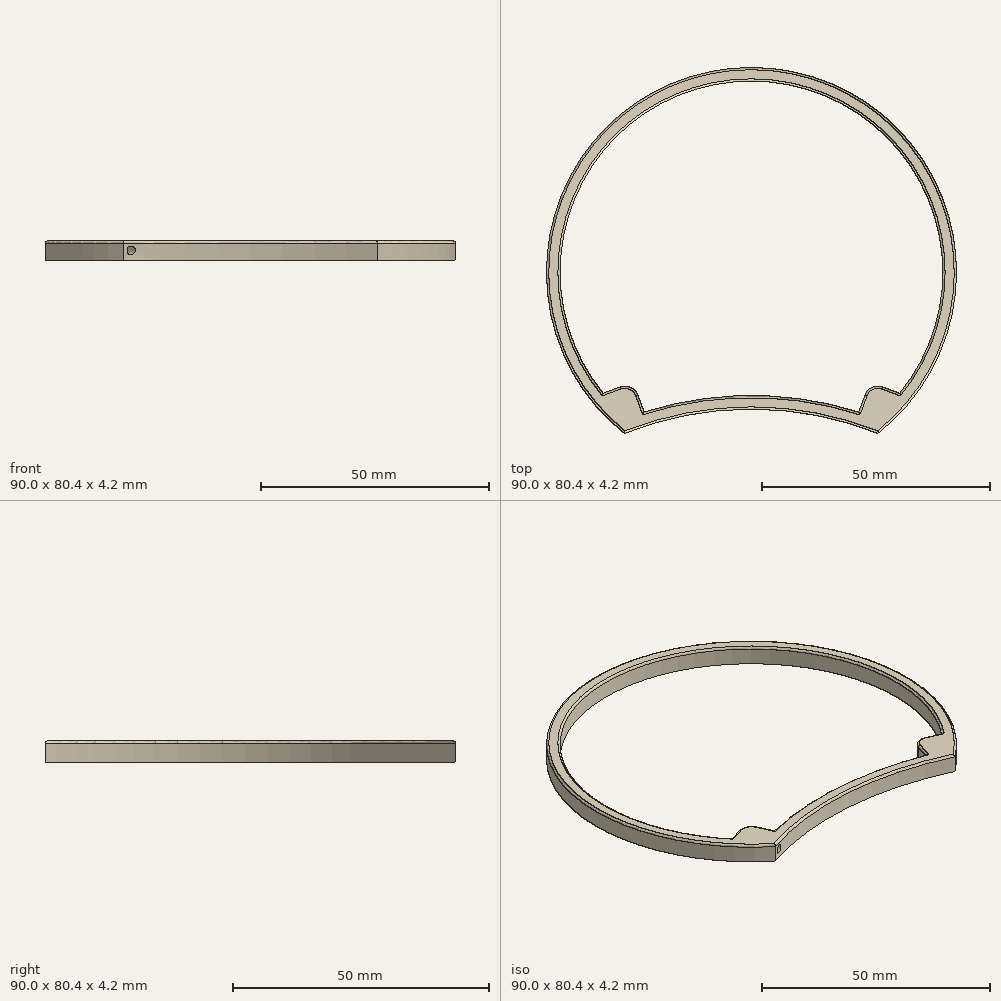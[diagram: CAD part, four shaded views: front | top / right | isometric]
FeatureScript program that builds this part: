
annotation { "Feature Type Name" : "Feature", "Feature Type Description" : "" }
export const myFeature = defineFeature(function(context is Context, id is Id, definition is map)
    precondition{}
    {
        {
            var Q0;
            Q0=qCreatedBy(makeId("Front.planeOp"),FACE);
            var sketch = newSketch(context, id + "F0", { "sketchPlane" : qUnion([Q0])});
            skLineSegment(sketch, "E0.bottom", {"start": v(42, 4.2) * mm, "end": v(45, 4.2) * mm});
            skLineSegment(sketch, "E0.top", {"start": v(42, 0) * mm, "end": v(45, 0) * mm});
            skLineSegment(sketch, "E0.left", {"start": v(42, 4.2) * mm, "end": v(42, 0) * mm});
            skLineSegment(sketch, "E0.right", {"start": v(45, 4.2) * mm, "end": v(45, 0) * mm});
            skLineSegment(sketch, "E1", {"start": v(0, 23.86) * mm, "end": v(0, -32.38) * mm, "construction": true});
            skSolve(sketch);
        }
        {
            var Q0;
            Q0=makeQuery(id+"F0.imprint","IMPRINT",FACE,{"disambiguationData":[TD([[makeQuery(id+"F0.imprint","IMPRINT",EDGE,{"derivedFrom":sQuery(id+"F0.wireOp",EDGE,"E0.bottom")}),-1.0]])]});
            var Q1;
            Q1=sQuery(id+"F0.wireOp",EDGE,"E1");
            revolve(context, id + "F1", {"surfaceOperationType" : NewSurfaceOperationType.NEW, "entities" : qUnion([Q0]), "axis" : qUnion([Q1]), "revolveType" : RevolveType.FULL});
        }
        {
            var Q0;
            Q0=qCreatedBy(makeId("Top.planeOp"),FACE);
            var sketch = newSketch(context, id + "F2", { "sketchPlane" : qUnion([Q0])});
            skCircle(sketch, "E2", {"center": v(0, -105) * mm, "radius": 78 * mm});
            skCircle(sketch, "E3.0", {"center": v(0, 0) * mm, "radius": 45 * mm});
            skCircle(sketch, "E4.0", {"center": v(0, 0) * mm, "radius": 42 * mm});
            skCircle(sketch, "E5.0", {"center": v(0, -105) * mm, "radius": 75 * mm});
            skSolve(sketch);
        }
        {
            var Q0;
            {var subQ0=sQuery(id+"F2.wireOp",EDGE,"E4.0");var subQ1=sQuery(id+"F2.wireOp",EDGE,"E2");var subQ2=makeQuery(id+"F2.imprint","INTERSECT",VERTEX,{"disambiguationData":[OD(0.0)],"derivedFrom":[subQ1,subQ0]});Q0=makeQuery(id+"F2.imprint","IMPRINT",FACE,{"disambiguationData":[TD([[makeQuery(id+"F2.imprint","IMPRINT",EDGE,{"disambiguationData":[TD([[subQ2,-1.0]])],"derivedFrom":subQ1}),1.0]])]});}
            var Q1;
            Q1=makeQuery(id+"F1.opRevolve","SWEPT_FACE",FACE,{"disambiguationData":[OSD([sQuery(id+"F0.wireOp",EDGE,"E0.bottom")])]});
            extrude(context, id + "F3", {"entities" : qUnion([Q0]), "operationType" : NewBodyOperationType.ADD, "endBound" : BoundingType.UP_TO_SURFACE, "depth" : 25 * mm, "endBoundEntityFace" : qUnion([Q1]), "offsetDistance" : 25 * mm});
        }
        {
            var Q0;
            {var subQ0=sQuery(id+"F2.wireOp",EDGE,"E5.0");var subQ1=sQuery(id+"F2.wireOp",EDGE,"E4.0");var subQ2=makeQuery(id+"F2.imprint","INTERSECT",VERTEX,{"disambiguationData":[OD(0.0)],"derivedFrom":[subQ1,subQ0]});Q0=makeQuery(id+"F2.imprint","IMPRINT",FACE,{"disambiguationData":[TD([[makeQuery(id+"F2.imprint","IMPRINT",EDGE,{"disambiguationData":[TD([[subQ2,-1.0]])],"derivedFrom":subQ1}),1.0]])]});}
            var Q1;
            {var subQ0=sQuery(id+"F2.wireOp",EDGE,"E5.0");var subQ1=sQuery(id+"F2.wireOp",EDGE,"E3.0");var subQ2=makeQuery(id+"F2.imprint","INTERSECT",VERTEX,{"disambiguationData":[OD(0.0)],"derivedFrom":[subQ1,subQ0]});Q1=makeQuery(id+"F2.imprint","IMPRINT",FACE,{"disambiguationData":[TD([[makeQuery(id+"F2.imprint","IMPRINT",EDGE,{"disambiguationData":[TD([[subQ2,-1.0]])],"derivedFrom":subQ1}),1.0]])]});}
            extrude(context, id + "F4", {"entities" : qUnion([Q0, Q1]), "operationType" : NewBodyOperationType.REMOVE, "depth" : 25 * mm, "offsetDistance" : 25 * mm});
        }
        {
            var Q0;
            Q0=qCreatedBy(makeId("Top.planeOp"),FACE);
            var sketch = newSketch(context, id + "F5", { "sketchPlane" : qUnion([Q0])});
            skArc(sketch, "E6.0", {"start": v(27.29, -31.93) * mm, "mid": v(0, 42) * mm, "end": v(-27.29, -31.93) * mm});
            skArc(sketch, "E6.1", {"start": v(27.29, -31.93) * mm, "mid": v(0, -27) * mm, "end": v(-27.29, -31.93) * mm});
            skLineSegment(sketch, "E7", {"start": v(-32.56, -26.53) * mm, "end": v(-26, -24.08) * mm});
            skLineSegment(sketch, "E8", {"start": v(-26, -24.08) * mm, "end": v(-23.55, -30.64) * mm});
            skLineSegment(sketch, "E9", {"start": v(-17.74, -28.37) * mm, "end": v(-42.66, -37.67) * mm, "construction": true});
            skLineSegment(sketch, "E10", {"start": v(0, 30.3) * mm, "end": v(0, -50.73) * mm, "construction": true});
            skLineSegment(sketch, "E11.MirrorCS", {"start": v(26, -24.08) * mm, "end": v(23.55, -30.64) * mm});
            skLineSegment(sketch, "E12.MirrorCS", {"start": v(32.56, -26.53) * mm, "end": v(26, -24.08) * mm});
            skSolve(sketch);
        }
        {
            var Q0;
            {var subQ0=sQuery(id+"F5.wireOp",EDGE,"E7");Q0=makeQuery(id+"F5.imprint","IMPRINT",FACE,{"disambiguationData":[TD([[makeQuery(id+"F5.imprint","IMPRINT",EDGE,{"derivedFrom":subQ0}),-1.0]])]});}
            var Q1;
            {var subQ4=sQuery(id+"F5.wireOp",EDGE,"E11.MirrorCS");Q1=makeQuery(id+"F5.imprint","IMPRINT",FACE,{"disambiguationData":[TD([[makeQuery(id+"F5.imprint","IMPRINT",EDGE,{"derivedFrom":subQ4}),1.0]])]});}
            var Q2;
            Q2=makeQuery(id+"F3.boolean.opBoolean","MERGE",FACE,{"derivedFrom":[makeQuery(id+"F1.opRevolve","SWEPT_FACE",FACE,{"disambiguationData":[OSD([sQuery(id+"F0.wireOp",EDGE,"E0.bottom")])]}),makeQuery(id+"F3.opExtrude","CAP_FACE",FACE,{"disambiguationData":[OSD([sQuery(id+"F2.wireOp",EDGE,"E2"),sQuery(id+"F2.wireOp",EDGE,"E4.0"),sQuery(id+"F2.wireOp",EDGE,"E5.0")])],"isStart":false})]});
            extrude(context, id + "F6", {"entities" : qUnion([Q0, Q1]), "operationType" : NewBodyOperationType.ADD, "endBound" : BoundingType.UP_TO_SURFACE, "depth" : 25 * mm, "endBoundEntityFace" : qUnion([Q2]), "offsetDistance" : 25 * mm});
        }
        {
            var Q0;
            Q0=makeQuery(id+"F6.opExtrude","SWEPT_EDGE",EDGE,{"disambiguationData":[OSD([sQuery(id+"F5.wireOp",EDGE,"E6.0"),sQuery(id+"F5.wireOp",EDGE,"E7")])]});
            var Q1;
            Q1=makeQuery(id+"F6.opExtrude","SWEPT_EDGE",EDGE,{"disambiguationData":[OSD([sQuery(id+"F5.wireOp",EDGE,"E7"),sQuery(id+"F5.wireOp",EDGE,"E8")])]});
            var Q2;
            Q2=makeQuery(id+"F6.opExtrude","SWEPT_EDGE",EDGE,{"disambiguationData":[OSD([sQuery(id+"F5.wireOp",EDGE,"E6.1"),sQuery(id+"F5.wireOp",EDGE,"E8")])]});
            var Q3;
            Q3=makeQuery(id+"F6.opExtrude","SWEPT_EDGE",EDGE,{"disambiguationData":[OSD([sQuery(id+"F5.wireOp",EDGE,"E11.MirrorCS"),sQuery(id+"F5.wireOp",EDGE,"E12.MirrorCS")])]});
            var Q4;
            Q4=makeQuery(id+"F6.opExtrude","SWEPT_EDGE",EDGE,{"disambiguationData":[OSD([sQuery(id+"F5.wireOp",EDGE,"E6.0"),sQuery(id+"F5.wireOp",EDGE,"E12.MirrorCS")])]});
            var Q5;
            Q5=makeQuery(id+"F6.opExtrude","SWEPT_EDGE",EDGE,{"disambiguationData":[OSD([sQuery(id+"F5.wireOp",EDGE,"E6.1"),sQuery(id+"F5.wireOp",EDGE,"E11.MirrorCS")])]});
            fillet(context, id + "F7", {"entities" : qUnion([Q0, Q1, Q2, Q3, Q4, Q5]), "tangentPropagation" : true, "radius" : 3 * mm, "defaultsChanged" : false, "vertexSettings" : [], "allowEdgeOverflow" : false});
        }
        {
            var Q0;
            Q0=makeQuery(id+"F6.opExtrude","SWEPT_FACE",FACE,{"disambiguationData":[OSD([sQuery(id+"F5.wireOp",EDGE,"E7")])]});
            var sketch = newSketch(context, id + "F8", { "sketchPlane" : qUnion([Q0])});
            skLineSegment(sketch, "E13", {"start": v(36.68, 0) * mm, "end": v(36.68, 4.2) * mm, "construction": true});
            skCircle(sketch, "E14", {"center": v(36.68, 2.1) * mm, "radius": 0.95 * mm});
            skSolve(sketch);
        }
        {
            var Q0;
            Q0 = qSketchRegion(id + "F8", true);
            var Q1;
            Q1 = qConstructionFilter(qBodyType(qCreatedBy(id + "F8" ,EDGE), BodyType.WIRE), ConstructionObject.NO);
            extrude(context, id + "F9", {"entities" : qUnion([Q0]), "operationType" : NewBodyOperationType.REMOVE, "surfaceEntities" : qUnion([Q1]), "oppositeDirection" : true, "depth" : 25 * mm, "offsetDistance" : 25 * mm});
        }
        {
            var Q0;
            Q0=makeQuery(id+"F1.opRevolve","SWEPT_FACE",FACE,{"disambiguationData":[OSD([sQuery(id+"F0.wireOp",EDGE,"E0.bottom")])]});
            fillet(context, id + "F10", {"entities" : qUnion([Q0]), "tangentPropagation" : true, "radius" : 0.5 * mm, "defaultsChanged" : true, "vertexSettings" : [], "allowEdgeOverflow" : false});
        }
    });
